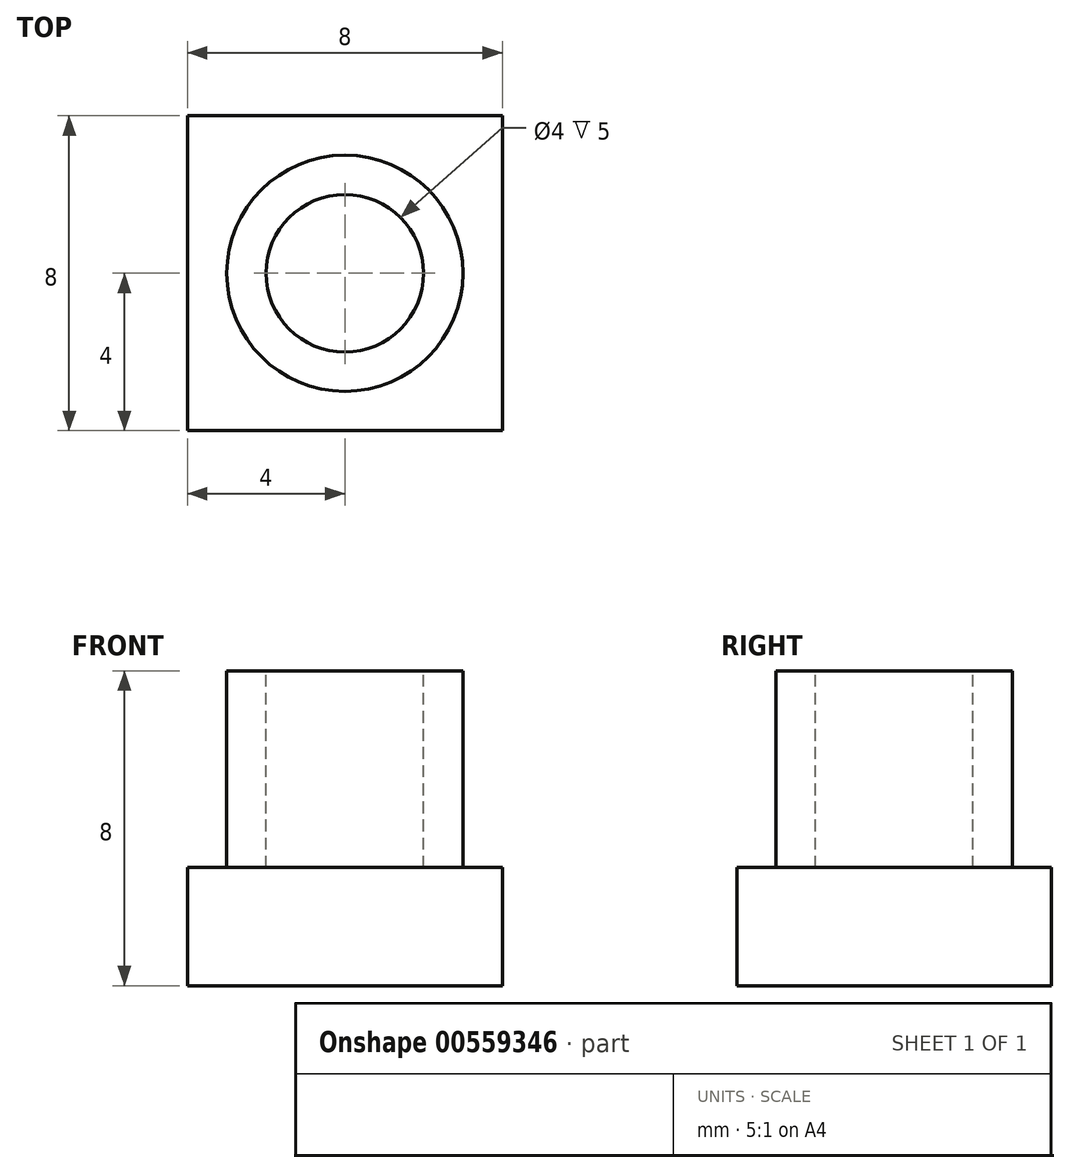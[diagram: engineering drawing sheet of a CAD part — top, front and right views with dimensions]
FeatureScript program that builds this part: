
annotation { "Feature Type Name" : "Feature", "Feature Type Description" : "" }
export const myFeature = defineFeature(function(context is Context, id is Id, definition is map)
    precondition{}
    {
        {
            var Q0;
            Q0=qCreatedBy(makeId("Top.planeOp"),FACE);
            var sketch = newSketch(context, id + "F0", { "sketchPlane" : qUnion([Q0])});
            skLineSegment(sketch, "E0.bottom", {"start": v(4, -4) * mm, "end": v(-4, -4) * mm});
            skLineSegment(sketch, "E0.top", {"start": v(4, 4) * mm, "end": v(-4, 4) * mm});
            skLineSegment(sketch, "E0.left", {"start": v(4, -4) * mm, "end": v(4, 4) * mm});
            skLineSegment(sketch, "E0.right", {"start": v(-4, -4) * mm, "end": v(-4, 4) * mm});
            skPoint(sketch, "E0.middle", {"position": v(0, 0) * mm});
            skSolve(sketch);
        }
        {
            var Q0;
            Q0=makeQuery(id+"F0.imprint","IMPRINT",FACE,{"disambiguationData":[TD([[makeQuery(id+"F0.imprint","IMPRINT",EDGE,{"derivedFrom":sQuery(id+"F0.wireOp",EDGE,"E0.bottom")}),-1.0]])]});
            extrude(context, id + "F1", {"entities" : qUnion([Q0]), "depth" : 3 * mm, "offsetDistance" : 25 * mm});
        }
        {
            var Q0;
            Q0=makeQuery(id+"F1.opExtrude","CAP_FACE",FACE,{"disambiguationData":[OSD([sQuery(id+"F0.wireOp",EDGE,"E0.bottom"),sQuery(id+"F0.wireOp",EDGE,"E0.top"),sQuery(id+"F0.wireOp",EDGE,"E0.left"),sQuery(id+"F0.wireOp",EDGE,"E0.right")])],"isStart":false});
            var sketch = newSketch(context, id + "F2", { "sketchPlane" : qUnion([Q0])});
            skCircle(sketch, "E1", {"center": v(0, 0) * mm, "radius": 3 * mm});
            skSolve(sketch);
        }
        {
            var Q0;
            Q0=makeQuery(id+"F2.imprint","IMPRINT",FACE,{"disambiguationData":[TD([[makeQuery(id+"F2.imprint","IMPRINT",EDGE,{"derivedFrom":sQuery(id+"F2.wireOp",EDGE,"E1")}),1.0]])]});
            extrude(context, id + "F3", {"entities" : qUnion([Q0]), "operationType" : NewBodyOperationType.ADD, "depth" : 5 * mm, "offsetDistance" : 25 * mm});
        }
        {
            var Q0;
            Q0=makeQuery(id+"F3.opExtrude","CAP_FACE",FACE,{"disambiguationData":[OSD([sQuery(id+"F2.wireOp",EDGE,"E1")])],"isStart":false});
            var sketch = newSketch(context, id + "F4", { "sketchPlane" : qUnion([Q0])});
            skCircle(sketch, "E2", {"center": v(0, 0) * mm, "radius": 2 * mm});
            skSolve(sketch);
        }
        {
            var Q0;
            Q0 = qSketchRegion(id + "F4", true);
            extrude(context, id + "F5", {"entities" : qUnion([Q0]), "operationType" : NewBodyOperationType.REMOVE, "oppositeDirection" : true, "depth" : 5 * mm, "offsetDistance" : 25 * mm});
        }
    });
